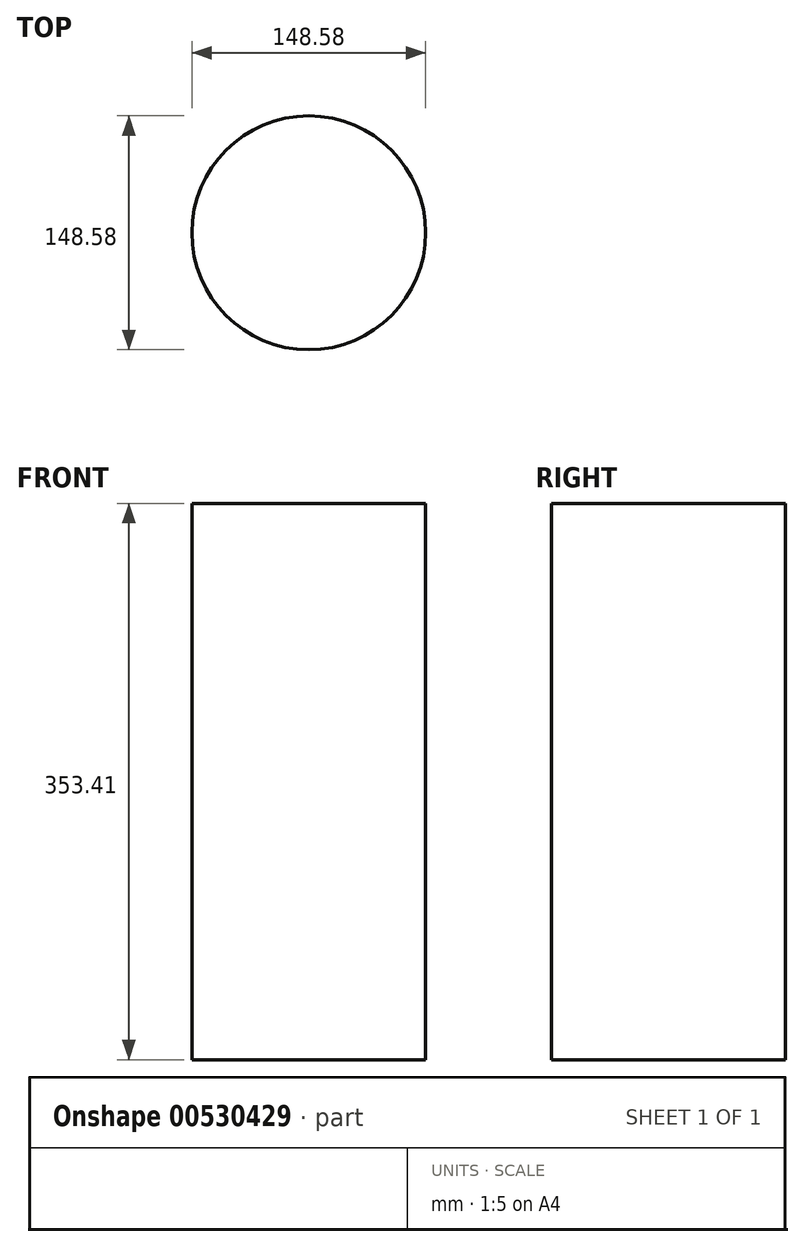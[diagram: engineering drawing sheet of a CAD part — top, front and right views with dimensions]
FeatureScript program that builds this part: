
annotation { "Feature Type Name" : "Feature", "Feature Type Description" : "" }
export const myFeature = defineFeature(function(context is Context, id is Id, definition is map)
    precondition{}
    {
        {
            var Q0;
            Q0=qCreatedBy(makeId("Front.planeOp"),FACE);
            var sketch = newSketch(context, id + "F0", { "sketchPlane" : qUnion([Q0])});
            skArc(sketch, "E0", {"start": v(-0.17, 70.47) * mm, "mid": v(52.42, 49.41) * mm, "end": v(75.1, -2.5) * mm});
            skArc(sketch, "E1", {"start": v(-0.17, 70.47) * mm, "mid": v(-52.58, 48.38) * mm, "end": v(-74.23, -4.2) * mm});
            skSolve(sketch);
        }
        {
            var Q0;
            Q0=qCreatedBy(makeId("Right.planeOp"),FACE);
            var sketch = newSketch(context, id + "F1", { "sketchPlane" : qUnion([Q0])});
            skArc(sketch, "E2", {"start": v(74.17, -2.35) * mm, "mid": v(0.44, 71.35) * mm, "end": v(-73.49, -2.15) * mm});
            skSolve(sketch);
        }
        {
            var Q0;
            Q0=qCreatedBy(makeId("Top.planeOp"),FACE);
            var sketch = newSketch(context, id + "F2", { "sketchPlane" : qUnion([Q0])});
            skCircle(sketch, "E3", {"center": v(0.34, 1.08) * mm, "radius": 74.29 * mm});
            skSolve(sketch);
        }
        {
            var Q0;
            Q0=makeQuery(id+"F2.imprint","IMPRINT",FACE,{"disambiguationData":[TD([[makeQuery(id+"F2.imprint","IMPRINT",EDGE,{"derivedFrom":sQuery(id+"F2.wireOp",EDGE,"E3")}),1.0]])]});
            var sketch = newSketch(context, id + "F3", { "sketchPlane" : qUnion([Q0])});
            skLineSegment(sketch, "E4.0", {"start": v(0, 74.17) * mm, "end": v(0, -73.49) * mm});
            skLineSegment(sketch, "E5.0", {"start": v(-0.17, 0) * mm, "end": v(75.1, 0) * mm});
            skLineSegment(sketch, "E6.0", {"start": v(-0.17, 0) * mm, "end": v(-74.23, 0) * mm});
            skCircle(sketch, "E7.0", {"center": v(0.34, 1.08) * mm, "radius": 74.29 * mm});
            skSolve(sketch);
        }
        {
            var Q0;
            Q0=makeQuery(id+"F2.imprint","IMPRINT",FACE,{"disambiguationData":[TD([[makeQuery(id+"F2.imprint","IMPRINT",EDGE,{"derivedFrom":sQuery(id+"F2.wireOp",EDGE,"E3")}),1.0]])]});
            extrude(context, id + "F4", {"entities" : qUnion([Q0]), "oppositeDirection" : true, "depth" : 68.81 * mm, "offsetDistance" : 25.4 * mm});
        }
        {
            var Q0;
            {var subQ0=sQuery(id+"F3.wireOp",EDGE,"E7.0");var subQ1=sQuery(id+"F3.wireOp",EDGE,"E4.0");var subQ2=makeQuery(id+"F3.imprint","INTERSECT",VERTEX,{"derivedFrom":[subQ1,subQ0]});Q0=makeQuery(id+"F3.imprint","IMPRINT",FACE,{"disambiguationData":[TD([[makeQuery(id+"F3.imprint","IMPRINT",EDGE,{"disambiguationData":[TD([[subQ2,1.0]])],"derivedFrom":subQ1}),-1.0]])]});}
            var Q1;
            {var subQ0=sQuery(id+"F3.wireOp",EDGE,"E6.0");var subQ1=sQuery(id+"F3.wireOp",EDGE,"E5.0");var subQ2=makeQuery(id+"F3.imprint","INTERSECT",VERTEX,{"derivedFrom":[subQ1,subQ0]});Q1=makeQuery(id+"F3.imprint","IMPRINT",FACE,{"disambiguationData":[TD([[makeQuery(id+"F3.imprint","IMPRINT",EDGE,{"disambiguationData":[TD([[subQ2,-1.0]])],"derivedFrom":subQ1}),1.0]])]});}
            var Q2;
            {var subQ0=sQuery(id+"F3.wireOp",EDGE,"E7.0");var subQ1=sQuery(id+"F3.wireOp",EDGE,"E4.0");var subQ2=makeQuery(id+"F3.imprint","INTERSECT",VERTEX,{"derivedFrom":[subQ1,subQ0]});Q2=makeQuery(id+"F3.imprint","IMPRINT",FACE,{"disambiguationData":[TD([[makeQuery(id+"F3.imprint","IMPRINT",EDGE,{"disambiguationData":[TD([[subQ2,1.0]])],"derivedFrom":subQ1}),1.0]])]});}
            extrude(context, id + "F5", {"entities" : qUnion([Q0, Q1, Q2]), "operationType" : NewBodyOperationType.ADD, "depth" : 284.6 * mm, "offsetDistance" : 25.4 * mm});
        }
    });
